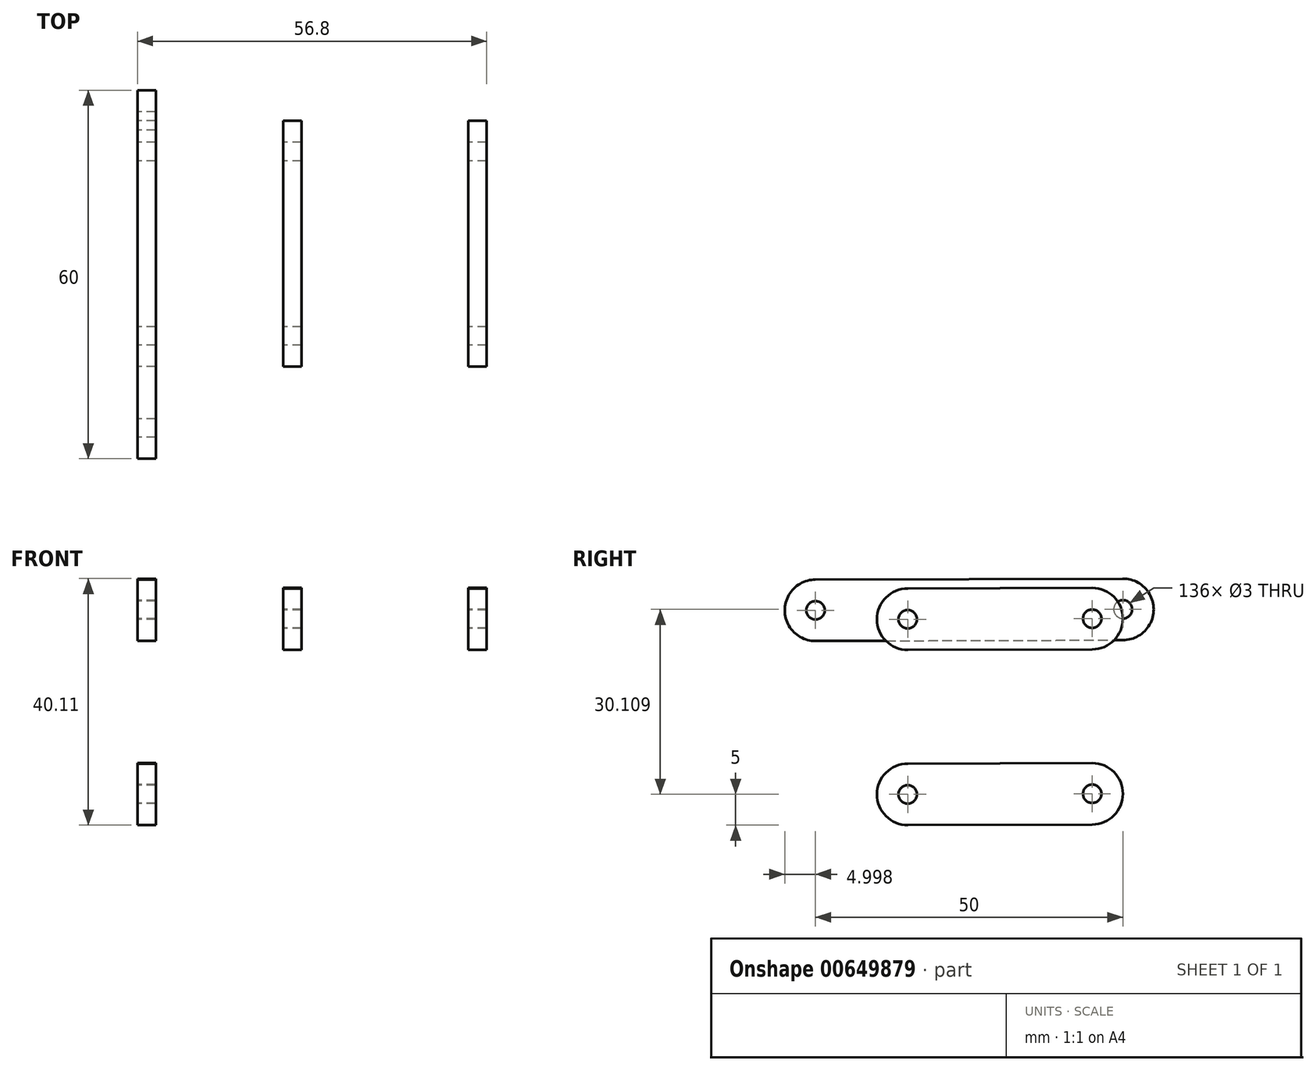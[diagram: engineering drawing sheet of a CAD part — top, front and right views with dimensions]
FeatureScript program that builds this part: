
annotation { "Feature Type Name" : "Feature", "Feature Type Description" : "" }
export const myFeature = defineFeature(function(context is Context, id is Id, definition is map)
    precondition{}
    {
        {
            var Q0;
            Q0=qCreatedBy(makeId("Right.planeOp"),FACE);
            var sketch = newSketch(context, id + "F0", { "sketchPlane" : qUnion([Q0])});
            skCircle(sketch, "E0", {"center": v(0, 0) * mm, "radius": 5 * mm});
            skCircle(sketch, "E1", {"center": v(30, 0.1) * mm, "radius": 5 * mm});
            skLineSegment(sketch, "E2", {"start": v(0, 5) * mm, "end": v(30, 5.1) * mm});
            skLineSegment(sketch, "E3", {"start": v(0, -5) * mm, "end": v(30.02, -4.9) * mm});
            skCircle(sketch, "E4", {"center": v(0, 0) * mm, "radius": 1.5 * mm});
            skCircle(sketch, "E5", {"center": v(30, 0.1) * mm, "radius": 1.5 * mm});
            skSolve(sketch);
        }
        {
            var Q0;
            Q0=makeQuery(id+"F0.imprint","IMPRINT",FACE,{"disambiguationData":[TD([[makeQuery(id+"F0.imprint","IMPRINT",EDGE,{"derivedFrom":sQuery(id+"F0.wireOp",EDGE,"E5")}),-1.0]])]});
            var Q1;
            {var subQ0=sQuery(id+"F0.wireOp",EDGE,"E2");Q1=makeQuery(id+"F0.imprint","IMPRINT",FACE,{"disambiguationData":[TD([[makeQuery(id+"F0.imprint","IMPRINT",EDGE,{"derivedFrom":subQ0}),-1.0]])]});}
            var Q2;
            Q2=makeQuery(id+"F0.imprint","IMPRINT",FACE,{"disambiguationData":[TD([[makeQuery(id+"F0.imprint","IMPRINT",EDGE,{"derivedFrom":sQuery(id+"F0.wireOp",EDGE,"E4")}),-1.0]])]});
            extrude(context, id + "F1", {"entities" : qUnion([Q0, Q1, Q2]), "depth" : 3 * mm, "offsetDistance" : 25 * mm});
        }
        {
            var Q0;
            Q0=makeQuery(id+"F1.opExtrude","SWEPT_BODY",BODY,{"disambiguationData":[OSD([sQuery(id+"F0.wireOp",EDGE,"E0"),sQuery(id+"F0.wireOp",EDGE,"E1"),sQuery(id+"F0.wireOp",EDGE,"E2"),sQuery(id+"F0.wireOp",EDGE,"E3"),sQuery(id+"F0.wireOp",EDGE,"E4"),sQuery(id+"F0.wireOp",EDGE,"E5")])]});
            transform(context, id + "F2", {"entities" : qUnion([Q0]), "transformType" : TransformType.TRANSLATION_3D, "dx" : 53.8 * mm, "dy" : 0 * mm, "dz" : 28.5 * mm, "makeCopy" : true});
        }
        {
            var Q0;
            Q0=makeQuery(id+"F2.opPattern","COPY",BODY,{"derivedFrom":makeQuery(id+"F1.opExtrude","SWEPT_BODY",BODY,{"disambiguationData":[OSD([sQuery(id+"F0.wireOp",EDGE,"E0"),sQuery(id+"F0.wireOp",EDGE,"E1"),sQuery(id+"F0.wireOp",EDGE,"E2"),sQuery(id+"F0.wireOp",EDGE,"E3"),sQuery(id+"F0.wireOp",EDGE,"E4"),sQuery(id+"F0.wireOp",EDGE,"E5")])]}),"instanceName":"1"});
            transform(context, id + "F3", {"entities" : qUnion([Q0]), "transformType" : TransformType.TRANSLATION_3D, "dx" : -30.1 * mm, "dy" : 0 * mm, "dz" : 0 * mm, "makeCopy" : true});
        }
        {
            var Q0;
            Q0=qCreatedBy(makeId("Right.planeOp"),FACE);
            var sketch = newSketch(context, id + "F4", { "sketchPlane" : qUnion([Q0])});
            skCircle(sketch, "E6", {"center": v(-15, 29.95) * mm, "radius": 5 * mm});
            skCircle(sketch, "E7", {"center": v(35, 30.1) * mm, "radius": 5 * mm});
            skLineSegment(sketch, "E8", {"start": v(-15, 34.95) * mm, "end": v(35, 35.1) * mm});
            skLineSegment(sketch, "E9", {"start": v(-15, 24.95) * mm, "end": v(35.01, 25.1) * mm});
            skCircle(sketch, "E10", {"center": v(-15, 29.95) * mm, "radius": 1.5 * mm});
            skCircle(sketch, "E11", {"center": v(35, 30.1) * mm, "radius": 1.5 * mm});
            skSolve(sketch);
        }
        {
            var Q0;
            Q0 = qSketchRegion(id + "F4", true);
            extrude(context, id + "F5", {"entities" : qUnion([Q0]), "depth" : 3 * mm, "offsetDistance" : 25 * mm});
        }
    });
